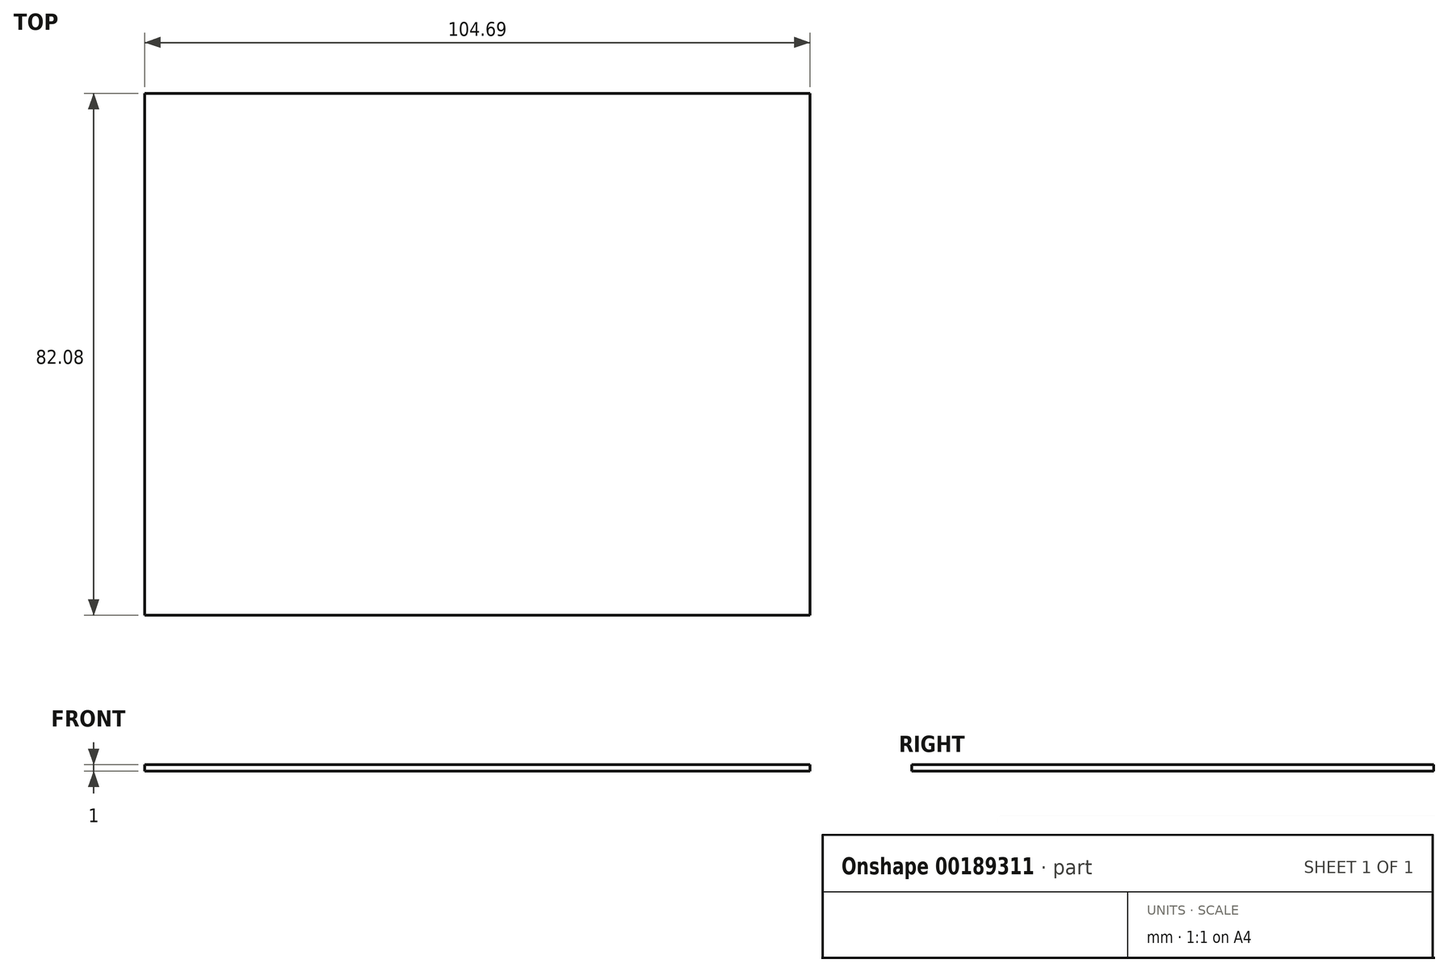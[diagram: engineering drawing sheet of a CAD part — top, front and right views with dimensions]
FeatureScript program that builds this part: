
annotation { "Feature Type Name" : "Feature", "Feature Type Description" : "" }
export const myFeature = defineFeature(function(context is Context, id is Id, definition is map)
    precondition{}
    {
        {
            var Q0;
            Q0=qCreatedBy(makeId("Top.planeOp"),FACE);
            var sketch = newSketch(context, id + "F0", { "sketchPlane" : qUnion([Q0])});
            skLineSegment(sketch, "E0.bottom", {"start": v(-54.53, 48.96) * mm, "end": v(50.16, 48.96) * mm});
            skLineSegment(sketch, "E0.top", {"start": v(-54.53, -33.12) * mm, "end": v(50.16, -33.12) * mm});
            skLineSegment(sketch, "E0.left", {"start": v(-54.53, 48.96) * mm, "end": v(-54.53, -33.12) * mm});
            skLineSegment(sketch, "E0.right", {"start": v(50.16, 48.96) * mm, "end": v(50.16, -33.12) * mm});
            skSolve(sketch);
        }
        {
            var Q0;
            Q0 = qSketchRegion(id + "F0", true);
            extrude(context, id + "F1", {"entities" : qUnion([Q0]), "depth" : 1 * mm});
        }
    });
